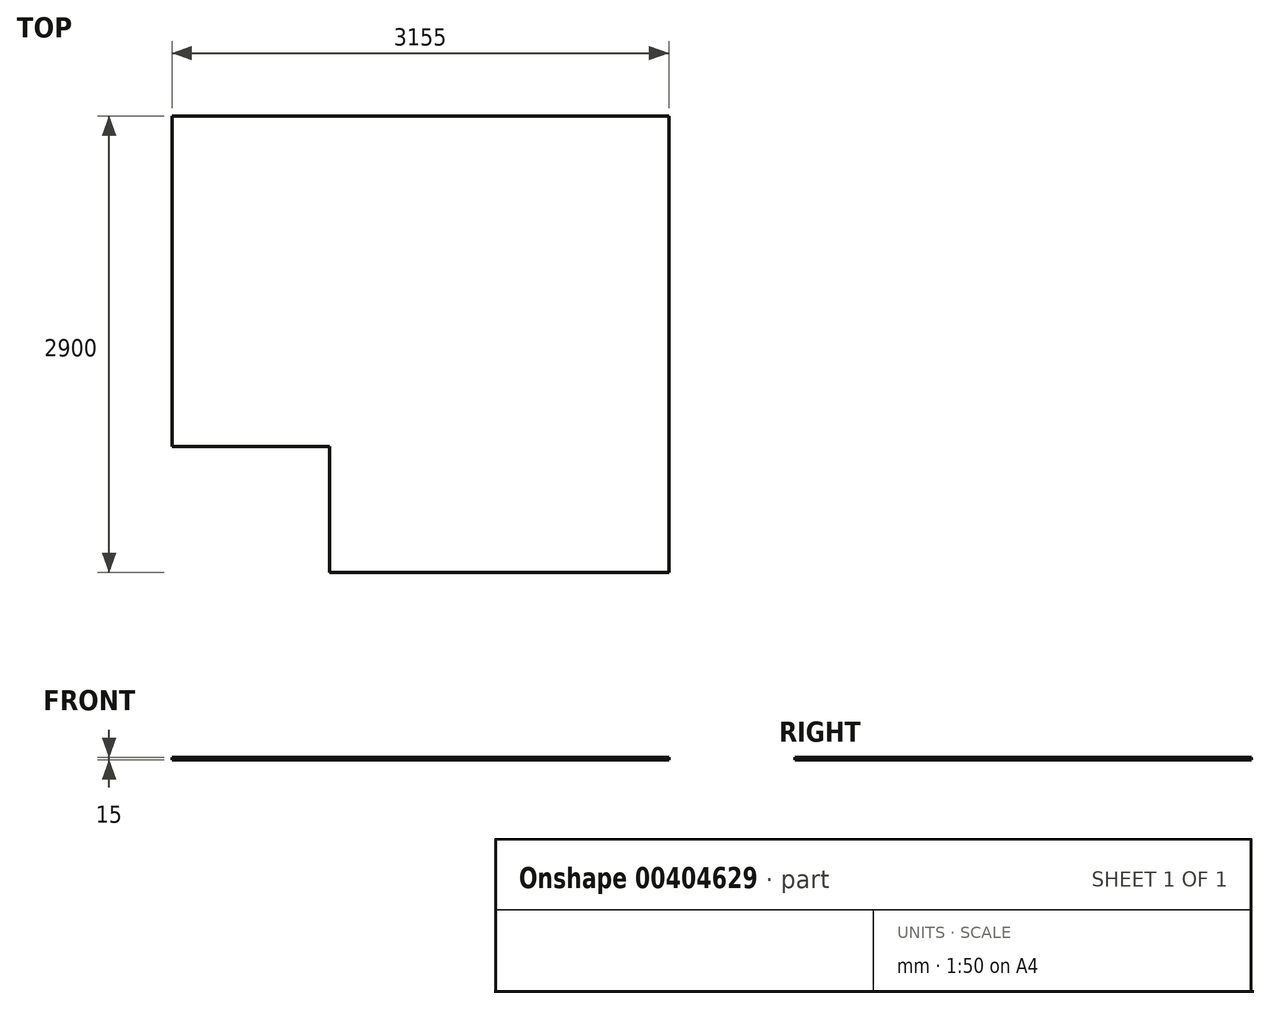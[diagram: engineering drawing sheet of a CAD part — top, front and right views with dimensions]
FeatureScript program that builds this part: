
annotation { "Feature Type Name" : "Feature", "Feature Type Description" : "" }
export const myFeature = defineFeature(function(context is Context, id is Id, definition is map)
    precondition{}
    {
        {
            var Q0;
            Q0=qCreatedBy(makeId("Top.planeOp"),FACE);
            var sketch = newSketch(context, id + "F0", { "sketchPlane" : qUnion([Q0])});
            skLineSegment(sketch, "E0", {"start": v(-1577.5, 1450) * mm, "end": v(-1577.5, -650) * mm});
            skLineSegment(sketch, "E1", {"start": v(-1577.5, -650) * mm, "end": v(-577.5, -650) * mm});
            skLineSegment(sketch, "E2", {"start": v(-577.5, -650) * mm, "end": v(-577.5, -1450) * mm});
            skLineSegment(sketch, "E3", {"start": v(-577.5, -1450) * mm, "end": v(1577.5, -1450) * mm});
            skLineSegment(sketch, "E4", {"start": v(1577.5, -1450) * mm, "end": v(1577.5, 1450) * mm});
            skLineSegment(sketch, "E5", {"start": v(1577.5, 1450) * mm, "end": v(-1577.5, 1450) * mm});
            skSolve(sketch);
        }
        {
            var Q0;
            Q0 = qSketchRegion(id + "F0", true);
            extrude(context, id + "F1", {"entities" : qUnion([Q0]), "depth" : 15 * mm});
        }
    });
